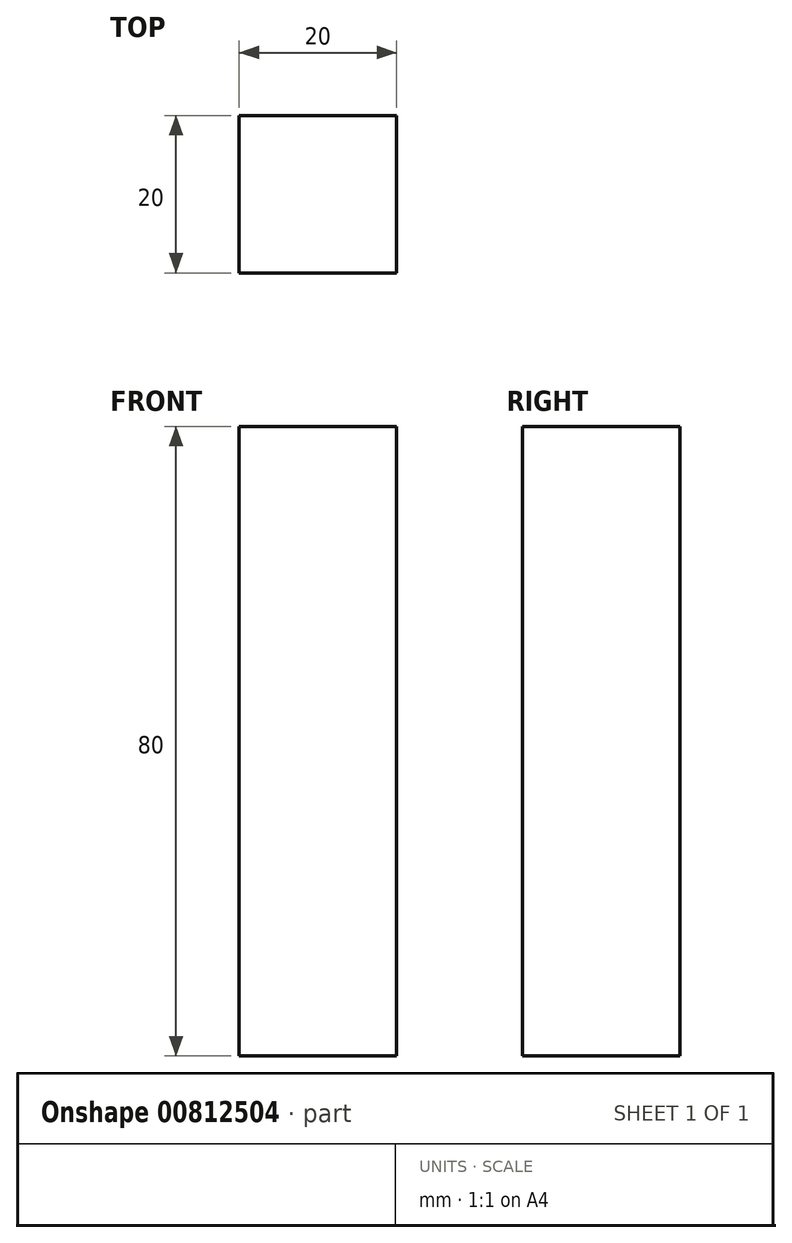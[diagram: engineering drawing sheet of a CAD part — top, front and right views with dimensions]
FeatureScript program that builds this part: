
annotation { "Feature Type Name" : "Feature", "Feature Type Description" : "" }
export const myFeature = defineFeature(function(context is Context, id is Id, definition is map)
    precondition{}
    {
        {
            var Q0;
            Q0=qCreatedBy(makeId("Top.planeOp"),FACE);
            var sketch = newSketch(context, id + "F0", { "sketchPlane" : qUnion([Q0])});
            skLineSegment(sketch, "E0.bottom", {"start": v(-10, 10) * mm, "end": v(10, 10) * mm});
            skLineSegment(sketch, "E0.top", {"start": v(-10, -10) * mm, "end": v(10, -10) * mm});
            skLineSegment(sketch, "E0.left", {"start": v(-10, 10) * mm, "end": v(-10, -10) * mm});
            skLineSegment(sketch, "E0.right", {"start": v(10, 10) * mm, "end": v(10, -10) * mm});
            skSolve(sketch);
        }
        {
            var Q0;
            Q0=makeQuery(id+"F0.imprint","IMPRINT",FACE,{"disambiguationData":[TD([[makeQuery(id+"F0.imprint","IMPRINT",EDGE,{"derivedFrom":sQuery(id+"F0.wireOp",EDGE,"E0.bottom")}),-1.0]])]});
            extrude(context, id + "F1", {"entities" : qUnion([Q0]), "endBound" : BoundingType.SYMMETRIC, "depth" : 80 * mm, "offsetDistance" : 25 * mm});
        }
    });
